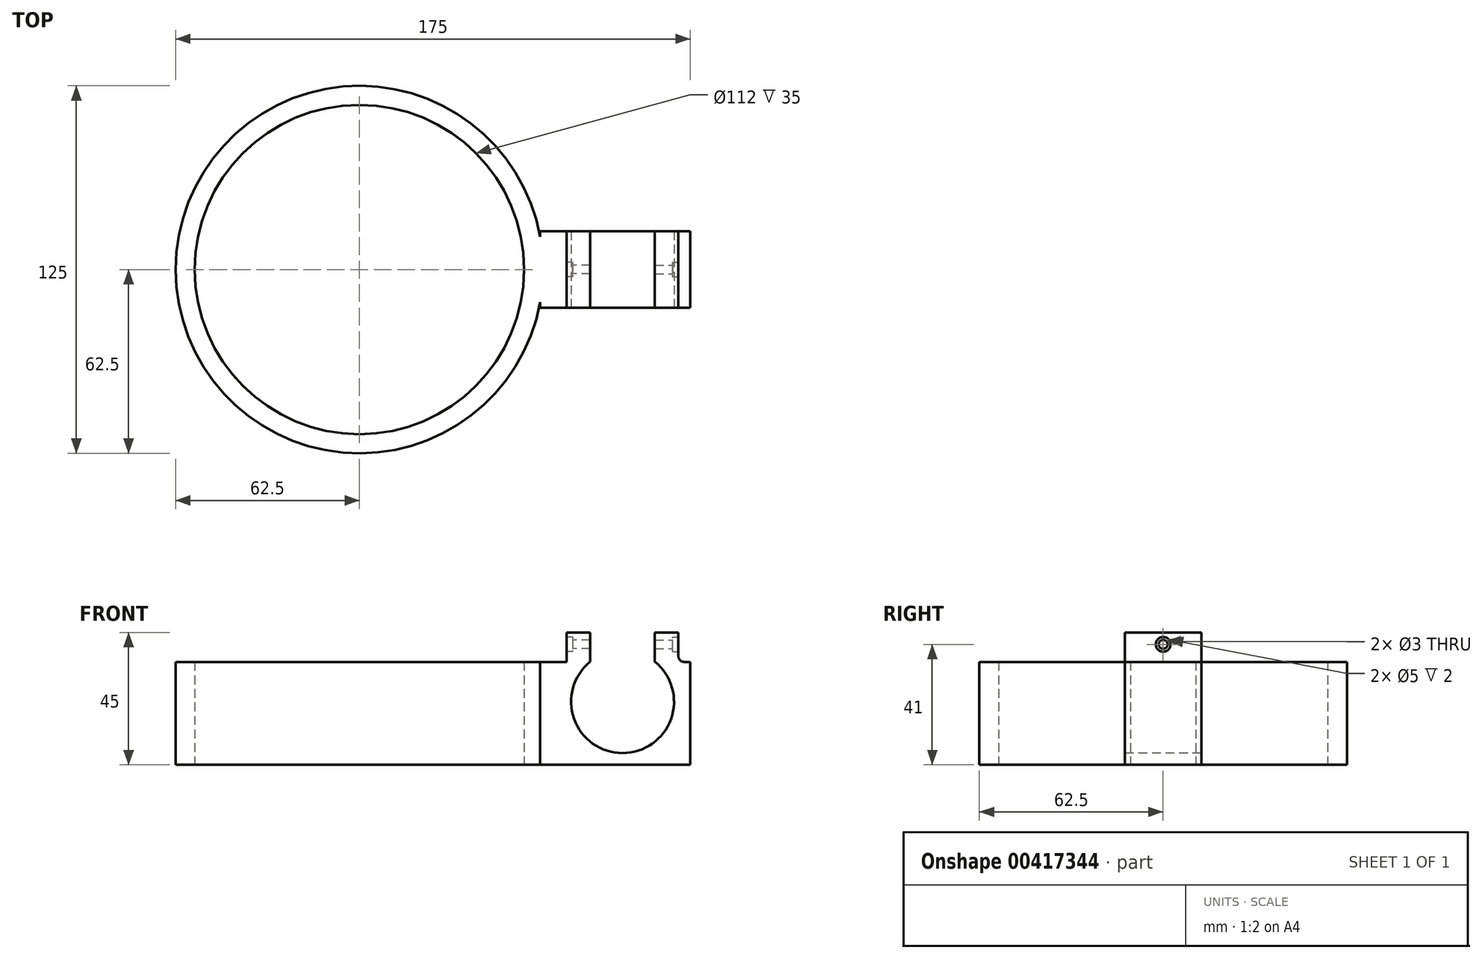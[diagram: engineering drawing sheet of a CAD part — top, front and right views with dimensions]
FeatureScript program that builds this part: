
annotation { "Feature Type Name" : "Feature", "Feature Type Description" : "" }
export const myFeature = defineFeature(function(context is Context, id is Id, definition is map)
    precondition{}
    {
        {
            var Q0;
            Q0=qCreatedBy(makeId("Top.planeOp"),FACE);
            var sketch = newSketch(context, id + "F0", { "sketchPlane" : qUnion([Q0])});
            skLineSegment(sketch, "E0", {"start": v(0, 0) * mm, "end": v(-62.5, 0) * mm});
            skCircle(sketch, "E1", {"center": v(-62.5, 0) * mm, "radius": 62.5 * mm});
            skCircle(sketch, "E2", {"center": v(-62.5, 0) * mm, "radius": 56 * mm});
            skSolve(sketch);
        }
        {
            var Q0;
            Q0 = qSketchRegion(id + "F0", true);
            extrude(context, id + "F1", {"entities" : qUnion([Q0]), "depth" : 35 * mm});
        }
        {
            var Q0;
            Q0=qCreatedBy(makeId("Right.planeOp"),FACE);
            var sketch = newSketch(context, id + "F2", { "sketchPlane" : qUnion([Q0])});
            skLineSegment(sketch, "E3", {"start": v(0, 0) * mm, "end": v(13, 0) * mm});
            skLineSegment(sketch, "E4", {"start": v(13, 0) * mm, "end": v(13, 35) * mm});
            skLineSegment(sketch, "E5", {"start": v(0, 0) * mm, "end": v(-13, 0) * mm});
            skLineSegment(sketch, "E6", {"start": v(-13, 0) * mm, "end": v(-13, 35) * mm});
            skLineSegment(sketch, "E7", {"start": v(-13, 35) * mm, "end": v(13, 35) * mm});
            skSolve(sketch);
        }
        {
            var Q0;
            Q0=makeQuery(id+"F2.imprint","IMPRINT",FACE,{"disambiguationData":[TD([[makeQuery(id+"F2.imprint","IMPRINT",EDGE,{"derivedFrom":sQuery(id+"F2.wireOp",EDGE,"E3")}),1.0]])]});
            extrude(context, id + "F3", {"entities" : qUnion([Q0]), "operationType" : NewBodyOperationType.ADD, "oppositeDirection" : true, "depth" : 1 * mm});
        }
        {
            var Q0;
            Q0=makeQuery(id+"F3.opExtrude","CAP_FACE",FACE,{"disambiguationData":[OSD([sQuery(id+"F2.wireOp",EDGE,"E3"),sQuery(id+"F2.wireOp",EDGE,"E4"),sQuery(id+"F2.wireOp",EDGE,"E5"),sQuery(id+"F2.wireOp",EDGE,"E6"),sQuery(id+"F2.wireOp",EDGE,"E7")])],"isStart":true});
            var sketch = newSketch(context, id + "F4", { "sketchPlane" : qUnion([Q0])});
            skLineSegment(sketch, "E8.bottom", {"start": v(-13, 35) * mm, "end": v(13, 35) * mm});
            skLineSegment(sketch, "E8.top", {"start": v(-13, 0) * mm, "end": v(13, 0) * mm});
            skLineSegment(sketch, "E8.left", {"start": v(-13, 35) * mm, "end": v(-13, 0) * mm});
            skLineSegment(sketch, "E8.right", {"start": v(13, 35) * mm, "end": v(13, 0) * mm});
            skSolve(sketch);
        }
        {
            var Q0;
            Q0 = qSketchRegion(id + "F4", true);
            extrude(context, id + "F5", {"entities" : qUnion([Q0]), "operationType" : NewBodyOperationType.ADD, "depth" : 50 * mm});
        }
        {
            var Q0;
            Q0=makeQuery(id+"F5.boolean.opBoolean","MERGE",FACE,{"derivedFrom":[makeQuery(id+"F3.opExtrude","SWEPT_FACE",FACE,{"disambiguationData":[OSD([sQuery(id+"F2.wireOp",EDGE,"E6")])]}),makeQuery(id+"F5.opExtrude","SWEPT_FACE",FACE,{"disambiguationData":[OSD([sQuery(id+"F4.wireOp",EDGE,"E8.left")])]})]});
            var sketch = newSketch(context, id + "F6", { "sketchPlane" : qUnion([Q0])});
            skLineSegment(sketch, "E9", {"start": v(50, 35) * mm, "end": v(46, 35) * mm});
            skLineSegment(sketch, "E10", {"start": v(46, 35) * mm, "end": v(46, 45) * mm});
            skLineSegment(sketch, "E11", {"start": v(46, 45) * mm, "end": v(38, 45) * mm});
            skLineSegment(sketch, "E12", {"start": v(38, 45) * mm, "end": v(38, 35) * mm});
            skLineSegment(sketch, "E13", {"start": v(38, 35) * mm, "end": v(46, 35) * mm});
            skLineSegment(sketch, "E14", {"start": v(-1, 35) * mm, "end": v(8, 35) * mm});
            skLineSegment(sketch, "E15", {"start": v(8, 35) * mm, "end": v(8, 45) * mm});
            skLineSegment(sketch, "E16", {"start": v(8, 45) * mm, "end": v(16, 45) * mm});
            skLineSegment(sketch, "E17", {"start": v(16, 45) * mm, "end": v(16, 35) * mm});
            skLineSegment(sketch, "E18", {"start": v(16, 35) * mm, "end": v(8, 35) * mm});
            skSolve(sketch);
        }
        {
            var Q0;
            Q0 = qSketchRegion(id + "F6", true);
            extrude(context, id + "F7", {"entities" : qUnion([Q0]), "operationType" : NewBodyOperationType.ADD, "oppositeDirection" : true, "depth" : 26 * mm});
        }
        {
            var Q0;
            Q0=makeQuery(id+"F7.boolean.opBoolean","MERGE",FACE,{"derivedFrom":[makeQuery(id+"F5.boolean.opBoolean","MERGE",FACE,{"derivedFrom":[makeQuery(id+"F3.opExtrude","SWEPT_FACE",FACE,{"disambiguationData":[OSD([sQuery(id+"F2.wireOp",EDGE,"E6")])]}),makeQuery(id+"F5.opExtrude","SWEPT_FACE",FACE,{"disambiguationData":[OSD([sQuery(id+"F4.wireOp",EDGE,"E8.left")])]})]}),makeQuery(id+"F7.opExtrude","CAP_FACE",FACE,{"disambiguationData":[OSD([sQuery(id+"F6.wireOp",EDGE,"E10"),sQuery(id+"F6.wireOp",EDGE,"E11"),sQuery(id+"F6.wireOp",EDGE,"E12"),sQuery(id+"F6.wireOp",EDGE,"E13")])],"isStart":true}),makeQuery(id+"F7.opExtrude","CAP_FACE",FACE,{"disambiguationData":[OSD([sQuery(id+"F6.wireOp",EDGE,"E15"),sQuery(id+"F6.wireOp",EDGE,"E16"),sQuery(id+"F6.wireOp",EDGE,"E17"),sQuery(id+"F6.wireOp",EDGE,"E18")])],"isStart":true})]});
            var sketch = newSketch(context, id + "F8", { "sketchPlane" : qUnion([Q0])});
            skLineSegment(sketch, "E19", {"start": v(38, 35) * mm, "end": v(27, 35) * mm});
            skLineSegment(sketch, "E20", {"start": v(27, 35) * mm, "end": v(27, 21.5) * mm});
            skCircle(sketch, "E21", {"center": v(27, 21.5) * mm, "radius": 17.5 * mm});
            skSolve(sketch);
        }
        {
            var Q0;
            Q0 = qSketchRegion(id + "F8", true);
            extrude(context, id + "F9", {"entities" : qUnion([Q0]), "operationType" : NewBodyOperationType.REMOVE, "oppositeDirection" : true, "depth" : 50 * mm});
        }
        {
            var Q0;
            Q0=makeQuery(id+"F7.opExtrude","SWEPT_EDGE",EDGE,{"disambiguationData":[OSD([sQuery(id+"F6.wireOp",EDGE,"E9"),sQuery(id+"F6.wireOp",EDGE,"E10"),sQuery(id+"F6.wireOp",EDGE,"E13")])]});
            var Q1;
            Q1=makeQuery(id+"F7.opExtrude","SWEPT_EDGE",EDGE,{"disambiguationData":[OSD([sQuery(id+"F6.wireOp",EDGE,"E14"),sQuery(id+"F6.wireOp",EDGE,"E15"),sQuery(id+"F6.wireOp",EDGE,"E18")])]});
            fillet(context, id + "F10", {"entities" : qUnion([Q0, Q1]), "radius" : 2 * mm, "tangentPropagation" : true, "allowEdgeOverflow" : false});
        }
        {
            var Q0;
            Q0=makeQuery(id+"F7.opExtrude","SWEPT_FACE",FACE,{"disambiguationData":[OSD([sQuery(id+"F6.wireOp",EDGE,"E10")])]});
            var sketch = newSketch(context, id + "F11", { "sketchPlane" : qUnion([Q0])});
            skLineSegment(sketch, "E22", {"start": v(13, 45) * mm, "end": v(0, 45) * mm});
            skLineSegment(sketch, "E23", {"start": v(0, 45) * mm, "end": v(0, 41) * mm});
            skPoint(sketch, "E23.endSnap0", {"position": v(0, 37) * mm});
            skCircle(sketch, "E24", {"center": v(0, 41) * mm, "radius": 1.5 * mm});
            skSolve(sketch);
        }
        {
            var Q0;
            Q0=sQuery(id+"F11.wireOp",VERTEX,"E23.end");
            var Q1;
            Q1=makeQuery(id+"F1.opExtrude","SWEPT_BODY",BODY,{"disambiguationData":[OSD([sQuery(id+"F0.wireOp",EDGE,"E1"),sQuery(id+"F0.wireOp",EDGE,"E2")])]});
            hole(context, id + "F12", {"style" : HoleStyle.C_BORE, "endStyle" : HoleEndStyle.BLIND, "holeDiameter" : 3 * mm, "cBoreDiameter" : 5 * mm, "cBoreDepth" : 2 * mm, "holeDepth" : 8 * mm, "isTappedThrough" : true, "tappedDepth" : 12 * mm, "tapClearance" : 3, "locations" : qUnion([Q0]), "scope" : qUnion([Q1])});
        }
        {
            var Q0;
            Q0=makeQuery(id+"F7.opExtrude","SWEPT_FACE",FACE,{"disambiguationData":[OSD([sQuery(id+"F6.wireOp",EDGE,"E15")])]});
            var sketch = newSketch(context, id + "F13", { "sketchPlane" : qUnion([Q0])});
            skLineSegment(sketch, "E25", {"start": v(13, 45) * mm, "end": v(0, 45) * mm});
            skLineSegment(sketch, "E26", {"start": v(0, 45) * mm, "end": v(0, 41) * mm});
            skSolve(sketch);
        }
        {
            var Q0;
            Q0=sQuery(id+"F13.wireOp",VERTEX,"E26.end");
            var Q1;
            Q1=makeQuery(id+"F1.opExtrude","SWEPT_BODY",BODY,{"disambiguationData":[OSD([sQuery(id+"F0.wireOp",EDGE,"E1"),sQuery(id+"F0.wireOp",EDGE,"E2")])]});
            hole(context, id + "F14", {"style" : HoleStyle.C_BORE, "endStyle" : HoleEndStyle.BLIND, "holeDiameter" : 3 * mm, "cBoreDiameter" : 5 * mm, "cBoreDepth" : 2 * mm, "holeDepth" : 8 * mm, "isTappedThrough" : true, "tappedDepth" : 12 * mm, "tapClearance" : 3, "locations" : qUnion([Q0]), "scope" : qUnion([Q1])});
        }
    });
